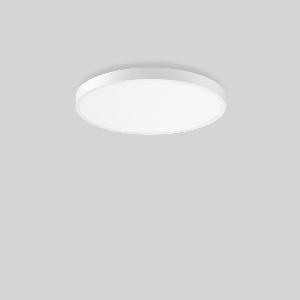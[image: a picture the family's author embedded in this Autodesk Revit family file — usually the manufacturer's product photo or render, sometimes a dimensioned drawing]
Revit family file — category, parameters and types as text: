
# Revit family: triona_round_a_312383_002_2_76_c4b0
name_source: partatom
category: Lighting Fixtures
units: mm (PartAtom-declared; Revit-internal decimal feet)

## family parameters
Cut with Voids When Loaded = No
Host = Face
Light Source = No
Part Type = Normal
Room Calculation Point = No
Round Connector Dimension = Use Diameter
Shared = No

## types (1)
- TuneableWhite 846 (1 x LED Modul 846, 3350 lm, 4600)
    Apparent Load = 40 VA
    CIE Flux Codes = 50 80 96 100 100
    Color Rendering = 80
    Color Temperature = 4600
    Default Elevation = 1800 mm
    Description = Series: TRIONA round
Decorative round LED surface-mounted luminaire. Flat, seamless frame: aluminium extrusion profile, powder coated. Cover made of sheet steel, powder-coated. Light emission through a diffuser: plastic, opal. Lightguide and diffuser made of non-yellowing plastic (PMMA). Lateral light emission (RZB SIDELITE technology) for above-average homogeneous light distribution. Tunable white versions, dynamically adjustable from 2700 K to 6500 K. Suitable for Ceiling mounting, Wall (surface). Tool-free mounting via bayonet connection. Electronic ballast included. Very easy installation thanks to Plug+Play connection. Ideal for use as part of the Human Centric Lighting concept in connection with RZB light management systems. 
Colour: traffic white, matt (RAL 9016)
Diameter: 681 mm
Height: 88 mm
Lamp: LED
Socket: without socket
Colour temperature: 2700K - 6500K
Colour rendering index (CRI): 80
System power: 40 W
Rated luminous flux: 3350 lm
Luminous efficiency: 84 lm/W
System power 2: 42 W
Rated luminous flux 2: 3200 lm
Luminous efficiency 2: 76 lm/W
System power 3: 42 W
Rated luminous flux 3: 3250 lm
Luminous efficiency 3: 77 lm/W
Control gear: Converter, dimmable, DALI
Protection class: I
Type of protection: IP 20
    Height = 88 mm
    Lamp = 1 x LED Modul 846
    Lamp Light Flux = 3350 lm
    Lamp count = 1
    Length = 681 mm
    Lifetime = 50000 h
    Luminous efficacy = 84 lm/W
    Manufacturer = RZB
    ModVariant = No
    Model = 312383.002.2.76
    Mounting Place = Ceiling
    Mounting Type = Surface mounted
    Number of Poles = 1
    OnlyDefault = Yes
    Power Factor = 1
    Product Name = TRIONA round A
    Product group = Surface mounted modular luminaires
    ProductGroupID = 306
    Protection Class = Protection class I
    Protection Degree = IP 20
    RLX_Detail_Level = 1
    RLX_Emergency_Light_Flux = 0 lm
    RLX_Emergency_Type = 0
    RLX_Emergency_Type_DB = No
    RlxData = <blob elided: 31645 chars, md5=e5d444f9>
    Socket = socket
    Standby Power = 0 W
    System Light Flux = 3350 lm
    System Power = 40 W
    Type Comments = TuneableWhite 846
    Type Image = 312384.002.jpg
    URL = http://relux.com
    VarID = tuneablewhite_846
    Voltage = 230 V
    Voltage Range = 220-240 V
    Weight = 0.00 kg
    Width = 0 mm  [stored 0 ft]

note: [stored X ft] marks values corroborated as IEEE doubles in the binary element streams (Revit-internal decimal feet)

## geometry (parser evidence)
native form markers: Blend x4, Sweep x9
no freeform markers — native parametric forms only
